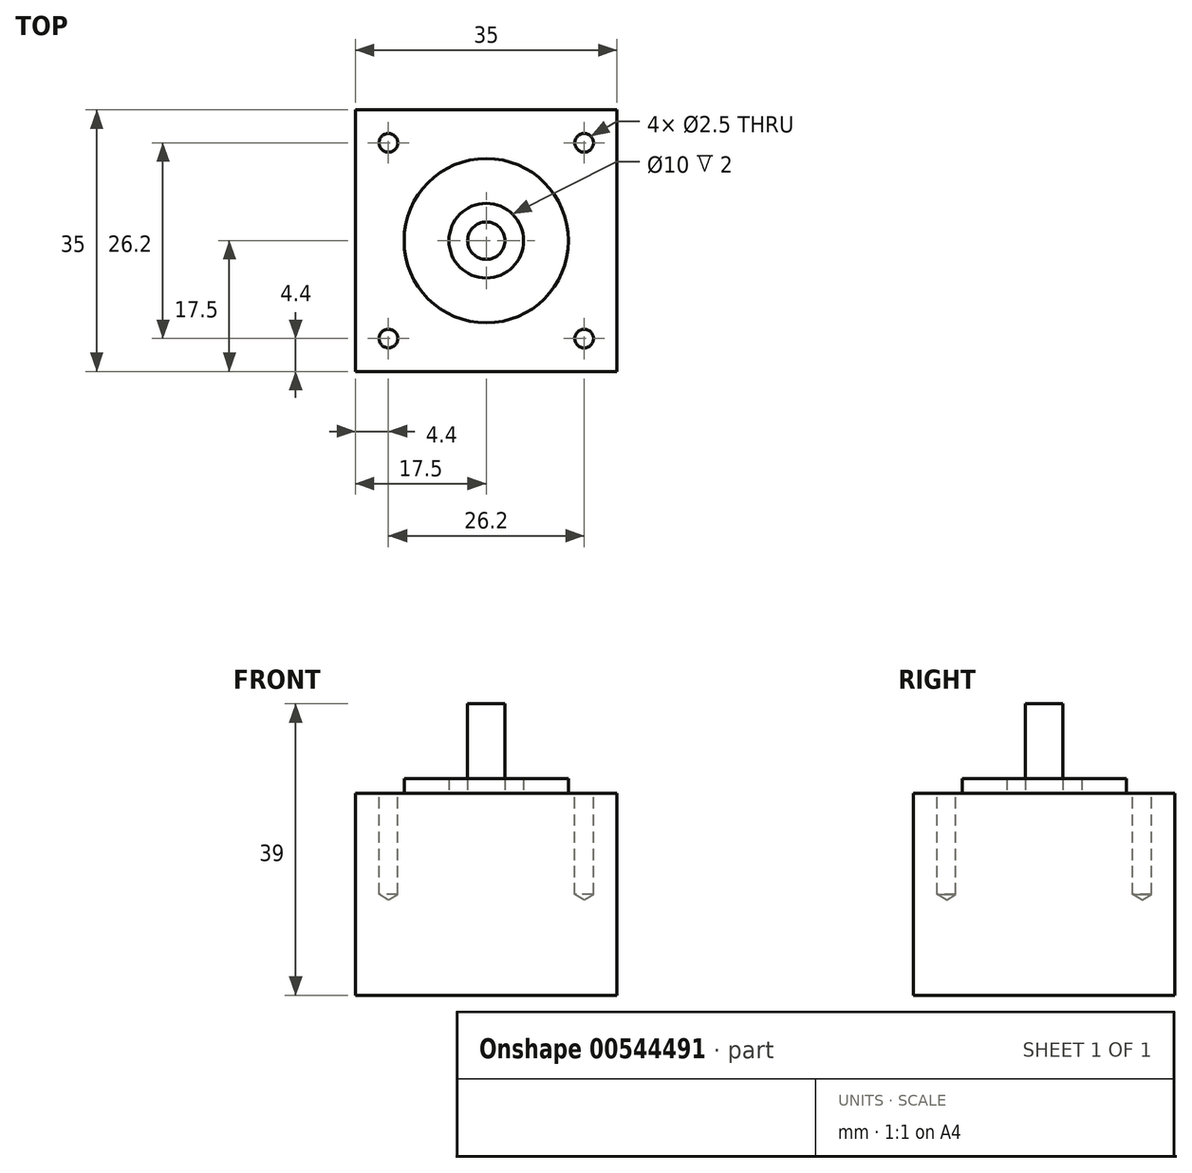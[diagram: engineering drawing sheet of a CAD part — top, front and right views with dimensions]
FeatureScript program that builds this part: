
annotation { "Feature Type Name" : "Feature", "Feature Type Description" : "" }
export const myFeature = defineFeature(function(context is Context, id is Id, definition is map)
    precondition{}
    {
        {
            var Q0;
            Q0=qCreatedBy(makeId("Top.planeOp"),FACE);
            var sketch = newSketch(context, id + "F0", { "sketchPlane" : qUnion([Q0])});
            skLineSegment(sketch, "E0.bottom", {"start": v(17.5, 17.5) * mm, "end": v(-17.5, 17.5) * mm});
            skLineSegment(sketch, "E0.top", {"start": v(17.5, -17.5) * mm, "end": v(-17.5, -17.5) * mm});
            skLineSegment(sketch, "E0.left", {"start": v(17.5, 17.5) * mm, "end": v(17.5, -17.5) * mm});
            skLineSegment(sketch, "E0.right", {"start": v(-17.5, 17.5) * mm, "end": v(-17.5, -17.5) * mm});
            skPoint(sketch, "E0.middle", {"position": v(0, 0) * mm});
            skSolve(sketch);
        }
        {
            var Q0;
            Q0=makeQuery(id+"F0.imprint","IMPRINT",FACE,{"disambiguationData":[TD([[makeQuery(id+"F0.imprint","IMPRINT",EDGE,{"derivedFrom":sQuery(id+"F0.wireOp",EDGE,"E0.bottom")}),1.0]])]});
            extrude(context, id + "F1", {"entities" : qUnion([Q0]), "depth" : 27 * mm, "offsetDistance" : 25 * mm});
        }
        {
            var Q0;
            Q0=makeQuery(id+"F1.opExtrude","CAP_FACE",FACE,{"disambiguationData":[OSD([sQuery(id+"F0.wireOp",EDGE,"E0.bottom"),sQuery(id+"F0.wireOp",EDGE,"E0.top"),sQuery(id+"F0.wireOp",EDGE,"E0.left"),sQuery(id+"F0.wireOp",EDGE,"E0.right")])],"isStart":false});
            var sketch = newSketch(context, id + "F2", { "sketchPlane" : qUnion([Q0])});
            skCircle(sketch, "E1", {"center": v(0, 0) * mm, "radius": 11 * mm});
            skCircle(sketch, "E2", {"center": v(0, 0) * mm, "radius": 5 * mm});
            skSolve(sketch);
        }
        {
            var Q0;
            Q0 = qSketchRegion(id + "F2", true);
            extrude(context, id + "F3", {"entities" : qUnion([Q0]), "operationType" : NewBodyOperationType.ADD, "depth" : 2 * mm, "offsetDistance" : 25 * mm});
        }
        {
            var Q0;
            Q0=makeQuery(id+"F3.boolean.opBoolean","SPLIT",FACE,{"disambiguationData":[TD([makeQuery(id+"F3.opExtrude","SWEPT_FACE",FACE,{"disambiguationData":[OSD([sQuery(id+"F2.wireOp",EDGE,"E2")])]})])],"derivedFrom":makeQuery(id+"F1.opExtrude","CAP_FACE",FACE,{"disambiguationData":[OSD([sQuery(id+"F0.wireOp",EDGE,"E0.bottom"),sQuery(id+"F0.wireOp",EDGE,"E0.top"),sQuery(id+"F0.wireOp",EDGE,"E0.left"),sQuery(id+"F0.wireOp",EDGE,"E0.right")])],"isStart":false})});
            var sketch = newSketch(context, id + "F4", { "sketchPlane" : qUnion([Q0])});
            skCircle(sketch, "E3", {"center": v(0, 0) * mm, "radius": 2.5 * mm});
            skSolve(sketch);
        }
        {
            var Q0;
            Q0 = qSketchRegion(id + "F4", true);
            extrude(context, id + "F5", {"entities" : qUnion([Q0]), "operationType" : NewBodyOperationType.ADD, "depth" : 12 * mm, "offsetDistance" : 25 * mm});
        }
        {
            var Q0;
            {var subQ0=sQuery(id+"F0.wireOp",EDGE,"E0.left");var subQ1=sQuery(id+"F0.wireOp",EDGE,"E0.top");var subQ2=sQuery(id+"F0.wireOp",EDGE,"E0.right");var subQ3=sQuery(id+"F0.wireOp",EDGE,"E0.bottom");Q0=makeQuery(id+"F3.boolean.opBoolean","SPLIT",FACE,{"disambiguationData":[TD([makeQuery(id+"F1.opExtrude","SWEPT_FACE",FACE,{"disambiguationData":[OSD([subQ3])]})])],"derivedFrom":makeQuery(id+"F1.opExtrude","CAP_FACE",FACE,{"disambiguationData":[OSD([subQ3,subQ1,subQ0,subQ2])],"isStart":false})});}
            var sketch = newSketch(context, id + "F6", { "sketchPlane" : qUnion([Q0])});
            skLineSegment(sketch, "E4.bottom", {"start": v(-13.1, 13.1) * mm, "end": v(13.1, 13.1) * mm});
            skLineSegment(sketch, "E4.top", {"start": v(-13.1, -13.1) * mm, "end": v(13.1, -13.1) * mm});
            skLineSegment(sketch, "E4.left", {"start": v(-13.1, 13.1) * mm, "end": v(-13.1, -13.1) * mm});
            skLineSegment(sketch, "E4.right", {"start": v(13.1, 13.1) * mm, "end": v(13.1, -13.1) * mm});
            skPoint(sketch, "E4.middle", {"position": v(0, 0) * mm});
            skSolve(sketch);
        }
        {
            var Q0;
            Q0=sQuery(id+"F6.wireOp",VERTEX,"E4.left.start");
            var Q1;
            Q1=sQuery(id+"F6.wireOp",VERTEX,"E4.right.start");
            var Q2;
            Q2=sQuery(id+"F6.wireOp",VERTEX,"E4.top.end");
            var Q3;
            Q3=sQuery(id+"F6.wireOp",VERTEX,"E4.left.end");
            var Q4;
            Q4=makeQuery(id+"F1.opExtrude","SWEPT_BODY",BODY,{"disambiguationData":[OSD([sQuery(id+"F0.wireOp",EDGE,"E0.bottom"),sQuery(id+"F0.wireOp",EDGE,"E0.top"),sQuery(id+"F0.wireOp",EDGE,"E0.left"),sQuery(id+"F0.wireOp",EDGE,"E0.right")])]});
            hole(context, id + "F7", {"style" : HoleStyle.SIMPLE, "endStyle" : HoleEndStyle.BLIND, "standardTappedOrClearance" : lookupTablePath({ "standard" : "ISO", "engagement" : "75%", "pitch" : "0.5 mm", "size" : "M3", "type" : "Tapped" }), "standardBlindInLast" : lookupTablePath({ "standard" : "ISO", "engagement" : "75%", "pitch" : "0.5 mm", "size" : "M3", "type" : "Tapped" }), "holeDiameter" : 2.5 * mm, "majorDiameter" : 3 * mm, "showTappedDepth" : true, "holeDepth" : 13.5 * mm, "tappedDepth" : 12 * mm, "tapClearance" : 3, "locations" : qUnion([Q0, Q1, Q2, Q3]), "scope" : qUnion([Q4])});
        }
    });
